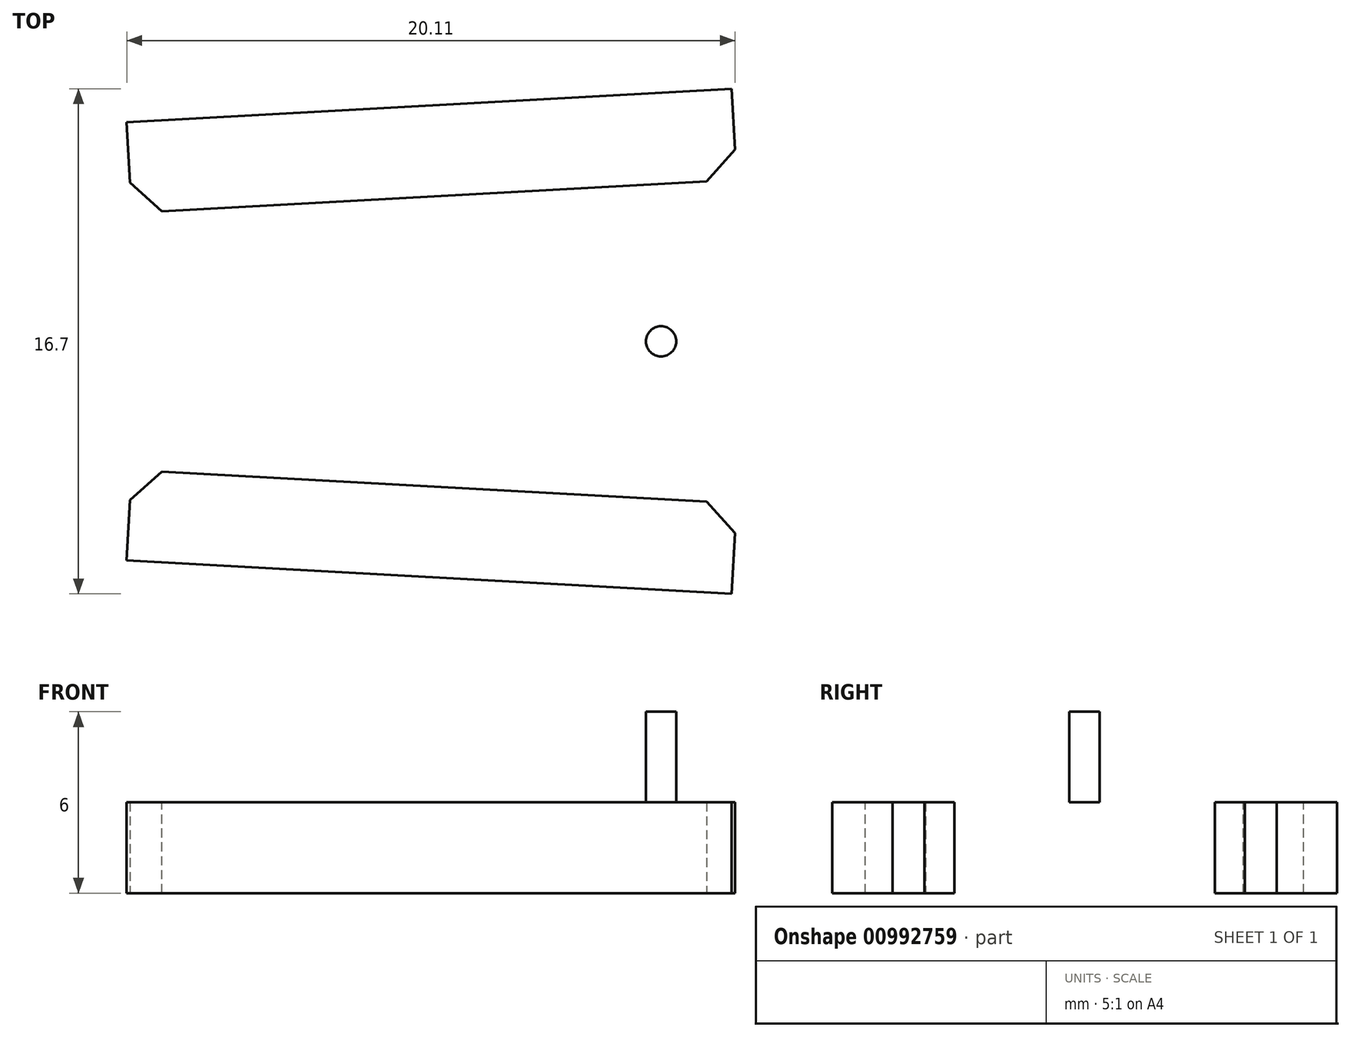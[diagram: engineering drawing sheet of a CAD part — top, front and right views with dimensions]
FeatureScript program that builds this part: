
annotation { "Feature Type Name" : "Feature", "Feature Type Description" : "" }
export const myFeature = defineFeature(function(context is Context, id is Id, definition is map)
    precondition{}
    {
        {
            var Q0;
            Q0=qCreatedBy(makeId("Top.planeOp"),FACE);
            var sketch = newSketch(context, id + "F0", { "sketchPlane" : qUnion([Q0])});
            skLineSegment(sketch, "E0", {"start": v(0, 0) * mm, "end": v(-10, 0) * mm, "construction": true});
            skLineSegment(sketch, "E1", {"start": v(-10, 0) * mm, "end": v(-10, -4.25) * mm, "construction": true});
            skLineSegment(sketch, "E2", {"start": v(0, 0) * mm, "end": v(10, 0) * mm, "construction": true});
            skLineSegment(sketch, "E3", {"start": v(10, 0) * mm, "end": v(10, -5.35) * mm, "construction": true});
            skLineSegment(sketch, "E4", {"start": v(-10, -4.25) * mm, "end": v(10, -5.35) * mm});
            skLineSegment(sketch, "E5.0", {"start": v(-10.16, -7.25) * mm, "end": v(9.84, -8.35) * mm});
            skLineSegment(sketch, "E6", {"start": v(-10, -4.25) * mm, "end": v(-10.16, -7.25) * mm});
            skLineSegment(sketch, "E7", {"start": v(10, -5.35) * mm, "end": v(9.84, -8.35) * mm});
            skLineSegment(sketch, "E8.MirrorCS", {"start": v(-10.16, 7.25) * mm, "end": v(9.84, 8.35) * mm});
            skLineSegment(sketch, "E9.MirrorCS", {"start": v(10, 5.35) * mm, "end": v(9.84, 8.35) * mm});
            skLineSegment(sketch, "E10.MirrorCS", {"start": v(-10, 4.25) * mm, "end": v(10, 5.35) * mm});
            skLineSegment(sketch, "E11.MirrorCS", {"start": v(-10, 4.25) * mm, "end": v(-10.16, 7.25) * mm});
            skSolve(sketch);
        }
        {
            var Q0;
            Q0=makeQuery(id+"F0.imprint","IMPRINT",FACE,{"disambiguationData":[TD([[makeQuery(id+"F0.imprint","IMPRINT",EDGE,{"derivedFrom":sQuery(id+"F0.wireOp",EDGE,"E4")}),-1.0]])]});
            var Q1;
            Q1=makeQuery(id+"F0.imprint","IMPRINT",FACE,{"disambiguationData":[TD([[makeQuery(id+"F0.imprint","IMPRINT",EDGE,{"derivedFrom":sQuery(id+"F0.wireOp",EDGE,"E8.MirrorCS")}),-1.0]])]});
            extrude(context, id + "F1", {"entities" : qUnion([Q0, Q1]), "oppositeDirection" : true, "depth" : 6 * mm, "offsetDistance" : 25 * mm});
        }
        {
            var Q0;
            Q0=makeQuery(id+"F1.opExtrude","CAP_FACE",FACE,{"disambiguationData":[OSD([sQuery(id+"F0.wireOp",EDGE,"E8.MirrorCS"),sQuery(id+"F0.wireOp",EDGE,"E9.MirrorCS"),sQuery(id+"F0.wireOp",EDGE,"E10.MirrorCS"),sQuery(id+"F0.wireOp",EDGE,"E11.MirrorCS")])],"isStart":true});
            var sketch = newSketch(context, id + "F2", { "sketchPlane" : qUnion([Q0])});
            skLineSegment(sketch, "E12", {"start": v(-10, 4.25) * mm, "end": v(10, 5.35) * mm});
            skLineSegment(sketch, "E13", {"start": v(10, 5.35) * mm, "end": v(10, -5.35) * mm});
            skLineSegment(sketch, "E14", {"start": v(-10, 4.25) * mm, "end": v(-10, -4.25) * mm});
            skLineSegment(sketch, "E15.MirrorCS", {"start": v(-10, -4.25) * mm, "end": v(10, -5.35) * mm});
            skSolve(sketch);
        }
        {
            var Q0;
            Q0=makeQuery(id+"F2.imprint","IMPRINT",FACE,{"disambiguationData":[TD([[makeQuery(id+"F2.imprint","IMPRINT",EDGE,{"derivedFrom":sQuery(id+"F2.wireOp",EDGE,"E12")}),-1.0]])]});
            extrude(context, id + "F3", {"entities" : qUnion([Q0]), "operationType" : NewBodyOperationType.ADD, "oppositeDirection" : true, "depth" : 3 * mm, "offsetDistance" : 25 * mm});
        }
        {
            var Q0;
            Q0=makeQuery(id+"F3.boolean.opBoolean","MERGE",FACE,{"derivedFrom":[makeQuery(id+"F1.opExtrude","CAP_FACE",FACE,{"disambiguationData":[OSD([sQuery(id+"F0.wireOp",EDGE,"E4"),sQuery(id+"F0.wireOp",EDGE,"E5.0"),sQuery(id+"F0.wireOp",EDGE,"E6"),sQuery(id+"F0.wireOp",EDGE,"E7")])],"isStart":true}),makeQuery(id+"F1.opExtrude","CAP_FACE",FACE,{"disambiguationData":[OSD([sQuery(id+"F0.wireOp",EDGE,"E8.MirrorCS"),sQuery(id+"F0.wireOp",EDGE,"E9.MirrorCS"),sQuery(id+"F0.wireOp",EDGE,"E10.MirrorCS"),sQuery(id+"F0.wireOp",EDGE,"E11.MirrorCS")])],"isStart":true}),makeQuery(id+"F3.opExtrude","CAP_FACE",FACE,{"disambiguationData":[OSD([sQuery(id+"F2.wireOp",EDGE,"E12"),sQuery(id+"F2.wireOp",EDGE,"E13"),sQuery(id+"F2.wireOp",EDGE,"E14"),sQuery(id+"F2.wireOp",EDGE,"E15.MirrorCS")])],"isStart":true})]});
            var sketch = newSketch(context, id + "F4", { "sketchPlane" : qUnion([Q0])});
            skLineSegment(sketch, "E16", {"start": v(0, 0) * mm, "end": v(-7.5, 0) * mm, "construction": true});
            skCircle(sketch, "E17", {"center": v(-7.5, 0) * mm, "radius": 0.5 * mm});
            skCircle(sketch, "E18.MirrorC", {"center": v(7.5, 0) * mm, "radius": 0.5 * mm});
            skSolve(sketch);
        }
        {
            var Q0;
            Q0=makeQuery(id+"F4.imprint","IMPRINT",FACE,{"disambiguationData":[TD([[makeQuery(id+"F4.imprint","IMPRINT",EDGE,{"derivedFrom":sQuery(id+"F4.wireOp",EDGE,"E17")}),1.0]])]});
            var Q1;
            Q1=makeQuery(id+"F4.imprint","IMPRINT",FACE,{"disambiguationData":[TD([[makeQuery(id+"F4.imprint","IMPRINT",EDGE,{"derivedFrom":sQuery(id+"F4.wireOp",EDGE,"E18.MirrorC")}),-1.0]])]});
            extrude(context, id + "F5", {"entities" : qUnion([Q0, Q1]), "operationType" : NewBodyOperationType.REMOVE, "oppositeDirection" : true, "depth" : 3 * mm, "offsetDistance" : 25 * mm});
        }
        {
            var Q0;
            Q0=makeQuery(id+"F3.boolean.opBoolean","SPLIT",EDGE,{"derivedFrom":makeQuery(id+"F1.opExtrude","SWEPT_EDGE",EDGE,{"disambiguationData":[OSD([sQuery(id+"F0.wireOp",EDGE,"E10.MirrorCS"),sQuery(id+"F0.wireOp",EDGE,"E11.MirrorCS")])]})});
            var Q1;
            Q1=makeQuery(id+"F3.boolean.opBoolean","SPLIT",EDGE,{"derivedFrom":makeQuery(id+"F1.opExtrude","SWEPT_EDGE",EDGE,{"disambiguationData":[OSD([sQuery(id+"F0.wireOp",EDGE,"E9.MirrorCS"),sQuery(id+"F0.wireOp",EDGE,"E10.MirrorCS")])]})});
            var Q2;
            Q2=makeQuery(id+"F3.boolean.opBoolean","SPLIT",EDGE,{"derivedFrom":makeQuery(id+"F1.opExtrude","SWEPT_EDGE",EDGE,{"disambiguationData":[OSD([sQuery(id+"F0.wireOp",EDGE,"E4"),sQuery(id+"F0.wireOp",EDGE,"E7")])]})});
            var Q3;
            Q3=makeQuery(id+"F3.boolean.opBoolean","SPLIT",EDGE,{"derivedFrom":makeQuery(id+"F1.opExtrude","SWEPT_EDGE",EDGE,{"disambiguationData":[OSD([sQuery(id+"F0.wireOp",EDGE,"E4"),sQuery(id+"F0.wireOp",EDGE,"E6")])]})});
            chamfer(context, id + "F6", {"entities" : qUnion([Q0, Q1, Q2, Q3]), "width" : 1 * mm, "tangentPropagation" : true});
        }
    });
